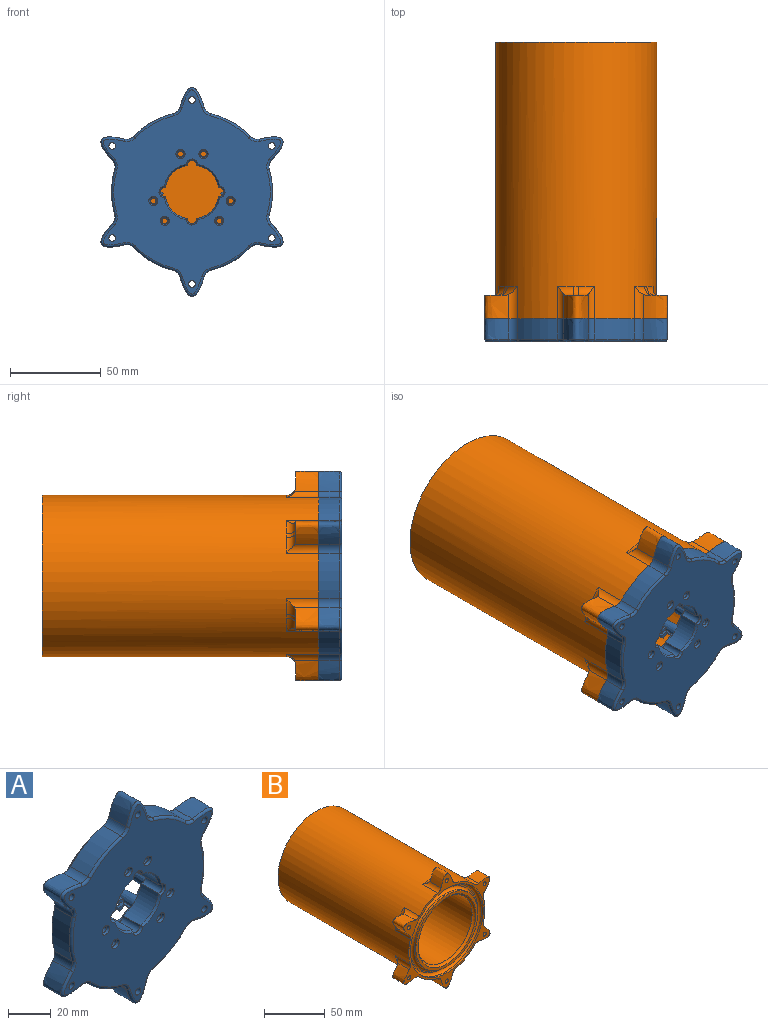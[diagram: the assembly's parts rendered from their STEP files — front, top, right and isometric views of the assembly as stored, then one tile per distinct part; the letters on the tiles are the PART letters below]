
ASSEMBLY  parts=2 mates=1
PART A: 221 faces, bbox 109.4x28x124.9 mm
  f0: plane 55.88x55.88mm, normal (0,1,0), area 1450.3mm2, adj f39,f42,f43,f44,f45,f46,f47,f48
  f1: cylinder r=44.45mm len=21.74mm, axis (0,-1,0), area 290.9mm2, adj f19,f21,f32,f78
  f2: extruded ~13.23x12.95mm, area 308.5mm2, adj f19,f21,f22,f74
  f3: cylinder r=44.45mm len=25.1mm, axis (0,-1,0), area 290.9mm2, adj f19,f22,f23,f70
  f4: extruded ~13.23x12.95mm, area 308.5mm2, adj f19,f23,f24,f66
  f5: cylinder r=44.45mm len=21.74mm, axis (0,-1,0), area 290.9mm2, adj f19,f24,f25,f62
  f6: extruded ~13.58x11.43mm, area 308.5mm2, adj f19,f25,f26,f58
  f7: cylinder r=44.45mm len=21.74mm, axis (0,-1,0), area 290.9mm2, adj f19,f26,f27,f57
  f8: extruded ~13.23x12.95mm, area 308.5mm2, adj f19,f27,f28,f61
  f9: cylinder r=44.45mm len=25.1mm, axis (0,-1,0), area 290.9mm2, adj f19,f28,f29,f65
  f10: extruded ~13.23x12.95mm, area 308.5mm2, adj f19,f29,f30,f69
  f11: cylinder r=44.45mm len=21.74mm, axis (0,-1,0), area 290.9mm2, adj f19,f30,f31,f73
  f12: cylinder r=1.84mm len=12.7mm, axis (0,-1,0), area 146.9mm2, adj f19,f20
  f13: cylinder r=1.84mm len=12.7mm, axis (0,-1,0), area 146.9mm2, adj f19,f20
  f14: cylinder r=1.84mm len=12.7mm, axis (0,-1,0), area 146.9mm2, adj f19,f20
  f15: cylinder r=1.84mm len=12.7mm, axis (0,-1,0), area 146.9mm2, adj f19,f20
  f16: cylinder r=1.84mm len=12.7mm, axis (0,-1,0), area 146.9mm2, adj f19,f20
  f17: extruded ~13.58x11.43mm, area 308.5mm2, adj f19,f31,f32,f77
  f18: cylinder r=1.84mm len=12.7mm, axis (0,-1,0), area 146.9mm2, adj f19,f20
  f19: plane 123.55x108.1mm, normal (0,1,0), area 1447.2mm2, adj f1,f2,f3,f4,f5,f6,f7,f8
  f20: plane 112.75x97.91mm, normal (0,-1,0), area 5549.7mm2, adj f12,f13,f14,f15,f16,f18,f56,f57
  f21: cylinder r=5.08mm len=11.43mm, axis (0,-1,0), area 60mm2, adj f1,f2,f19,f76
  f22: cylinder r=5.08mm len=11.43mm, axis (0,-1,0), area 60mm2, adj f2,f3,f19,f72
  f23: cylinder r=5.08mm len=11.43mm, axis (0,-1,0), area 60mm2, adj f3,f4,f19,f68
  f24: cylinder r=5.08mm len=11.43mm, axis (0,-1,0), area 60mm2, adj f4,f5,f19,f64
  f25: cylinder r=5.08mm len=11.43mm, axis (0,-1,0), area 60mm2, adj f5,f6,f19,f60
  f26: cylinder r=5.08mm len=11.43mm, axis (0,-1,0), area 60mm2, adj f6,f7,f19,f56
  f27: cylinder r=5.08mm len=11.43mm, axis (0,-1,0), area 60mm2, adj f7,f8,f19,f59
  f28: cylinder r=5.08mm len=11.43mm, axis (0,-1,0), area 60mm2, adj f8,f9,f19,f63
  f29: cylinder r=5.08mm len=11.43mm, axis (0,-1,0), area 60mm2, adj f9,f10,f19,f67
  f30: cylinder r=5.08mm len=11.43mm, axis (0,-1,0), area 60mm2, adj f10,f11,f19,f71
  f31: cylinder r=5.08mm len=11.43mm, axis (0,-1,0), area 60mm2, adj f11,f17,f19,f75
  f32: cylinder r=5.08mm len=11.43mm, axis (0,-1,0), area 60mm2, adj f1,f17,f19,f79
  f33: cylinder r=41.91mm len=83.82mm, axis (0,-1,0), area 200.7mm2, adj f19,f37
  f34: cylinder r=36.83mm len=73.66mm, axis (0,-1,0), area 176.3mm2, adj f36,f38
  f35: plane 78.99x78.99mm, normal (0,1,0), area 62.8mm2, adj f37,f38
  f36: plane 73.66x73.66mm, normal (0,1,0), area 1094.5mm2, adj f34,f40
  f37: torus R=39.5mm, axis (0,1,0), area 977.2mm2, adj f33,f35
  f38: torus R=39.24mm, axis (0,1,0), area 898mm2, adj f34,f35
  f39: cylinder r=27.94mm len=55.88mm, axis (0,-1,0), area 1783.6mm2, adj f0,f41
  f40: cylinder r=31.75mm len=63.5mm, axis (0,-1,0), area 1782.2mm2, adj f36,f220
  f41: plane 61.05x61.05mm, normal (0,1,0), area 474.5mm2, adj f39,f220
  f42: cylinder r=2.54mm len=11.43mm, axis (0,-1,0), area 96.2mm2, adj f0,f43,f49,f89
  f43: cylinder r=14.94mm len=12.19mm, axis (0,-1,0), area 210mm2, adj f0,f42,f44,f87
  f44: cylinder r=2.54mm len=11.43mm, axis (0,-1,0), area 96.2mm2, adj f0,f43,f45,f85
  f45: cylinder r=14.94mm len=12.19mm, axis (0,-1,0), area 210mm2, adj f0,f44,f46,f83
  f46: cylinder r=2.54mm len=11.43mm, axis (0,-1,0), area 96.2mm2, adj f0,f45,f47,f84
  f47: cylinder r=14.94mm len=12.19mm, axis (0,-1,0), area 210mm2, adj f0,f46,f48,f86
  f48: cylinder r=2.54mm len=11.43mm, axis (0,-1,0), area 96.2mm2, adj f0,f47,f49,f88
  f49: cylinder r=14.94mm len=12.19mm, axis (0,-1,0), area 210mm2, adj f0,f42,f48,f90
  f50: cylinder r=1.78mm len=11.43mm, axis (0,1,0), area 127.7mm2, adj f0,f80,f95
  f51: cylinder r=1.78mm len=11.43mm, axis (0,1,0), area 127.7mm2, adj f0,f92,f200
  f52: cylinder r=1.78mm len=11.43mm, axis (0,1,0), area 127.7mm2, adj f0,f91,f116
  f53: cylinder r=1.78mm len=11.43mm, axis (0,1,0), area 127.7mm2, adj f0,f82,f137
  f54: cylinder r=1.78mm len=11.43mm, axis (0,1,0), area 127.7mm2, adj f0,f81,f158
  f55: cylinder r=1.78mm len=11.43mm, axis (0,1,0), area 127.7mm2, adj f0,f93,f179
  f56: torus R=6.35mm, axis (0,-1,0), area 11.4mm2, adj f20,f26,f57,f58
  f57: torus R=43.18mm, axis (0,-1,0), area 50.2mm2, adj f7,f20,f56,f59
  f58: bspline ~14.43x12.79mm, area 51.6mm2, adj f6,f20,f56,f60
  f59: torus R=6.35mm, axis (0,-1,0), area 11.4mm2, adj f20,f27,f57,f61
  f60: torus R=6.35mm, axis (0,-1,0), area 11.4mm2, adj f20,f25,f58,f62
  f61: bspline ~14.68x14.01mm, area 51.6mm2, adj f8,f20,f59,f63
  f62: torus R=43.18mm, axis (0,-1,0), area 50.2mm2, adj f5,f20,f60,f64
  f63: torus R=6.35mm, axis (0,-1,0), area 11.4mm2, adj f20,f28,f61,f65
  f64: torus R=6.35mm, axis (0,-1,0), area 11.4mm2, adj f20,f24,f62,f66
  f65: torus R=43.18mm, axis (0,-1,0), area 50.2mm2, adj f9,f20,f63,f67
  f66: bspline ~14.04x13.58mm, area 51.6mm2, adj f4,f20,f64,f68
  f67: torus R=6.35mm, axis (0,-1,0), area 11.4mm2, adj f20,f29,f65,f69
  f68: torus R=6.35mm, axis (0,-1,0), area 11.4mm2, adj f20,f23,f66,f70
  f69: bspline ~14.04x13.58mm, area 51.6mm2, adj f10,f20,f67,f71
  f70: torus R=43.18mm, axis (0,-1,0), area 50.2mm2, adj f3,f20,f68,f72
  f71: torus R=6.35mm, axis (0,-1,0), area 11.4mm2, adj f20,f30,f69,f73
  f72: torus R=6.35mm, axis (0,-1,0), area 11.4mm2, adj f20,f22,f70,f74
  f73: torus R=43.18mm, axis (0,-1,0), area 50.2mm2, adj f11,f20,f71,f75
  f74: bspline ~14.01x13.59mm, area 51.6mm2, adj f2,f20,f72,f76
  f75: torus R=6.35mm, axis (0,-1,0), area 11.4mm2, adj f20,f31,f73,f77
  f76: torus R=6.35mm, axis (0,-1,0), area 11.4mm2, adj f20,f21,f74,f78
  f77: bspline ~14.43x12.79mm, area 51.6mm2, adj f17,f20,f75,f79
  f78: torus R=43.18mm, axis (0,-1,0), area 50.2mm2, adj f1,f20,f76,f79
  f79: torus R=6.35mm, axis (0,-1,0), area 11.4mm2, adj f20,f32,f77,f78
  f80: cone r=1.78mm half-angle=30deg, axis (0,-1,0), area 19.8mm2, adj f20,f50
  f81: cone r=1.78mm half-angle=30deg, axis (0,-1,0), area 19.8mm2, adj f20,f54
  f82: cone r=1.78mm half-angle=30deg, axis (0,-1,0), area 19.8mm2, adj f20,f53
  f83: cone r=14.94mm half-angle=30deg, axis (0,-1,0), area 26.7mm2, adj f20,f45,f84,f85
  f84: cone r=2.54mm half-angle=30deg, axis (0,-1,0), area 13.2mm2, adj f20,f46,f83,f86
  f85: cone r=2.54mm half-angle=30deg, axis (0,-1,0), area 13.2mm2, adj f20,f44,f83,f87
  f86: cone r=14.94mm half-angle=30deg, axis (0,-1,0), area 26.7mm2, adj f20,f47,f84,f88
  f87: cone r=14.94mm half-angle=30deg, axis (0,-1,0), area 26.7mm2, adj f20,f43,f85,f89
  f88: cone r=2.54mm half-angle=30deg, axis (0,-1,0), area 13.2mm2, adj f20,f48,f86,f90
  f89: cone r=2.54mm half-angle=30deg, axis (0,-1,0), area 13.2mm2, adj f20,f42,f87,f90
  f90: cone r=14.94mm half-angle=30deg, axis (0,-1,0), area 26.7mm2, adj f20,f49,f88,f89
  f91: cone r=1.78mm half-angle=30deg, axis (0,-1,0), area 19.8mm2, adj f20,f52
  f92: cone r=1.78mm half-angle=30deg, axis (0,-1,0), area 19.8mm2, adj f20,f51
  f93: cone r=1.78mm half-angle=30deg, axis (0,-1,0), area 19.8mm2, adj f20,f55
  f94: bspline ~13.97x7.67mm, area 268mm2, adj f0,f96,f97,f98,f106,f108,f109,f110
  f95: bspline ~13.97x3.58mm, area 87.4mm2, adj f50,f97,f98,f99,f100
  f96: plane 9.94x9.5mm, normal (0,1,0), area 32.9mm2, adj f94,f97,f98,f102,f103,f104,f105,f107
  f97: bspline ~13.97x1.99mm, area 24.9mm2, adj f0,f94,f95,f96,f101
  f98: bspline ~13.97x1.72mm, area 22.7mm2, adj f0,f94,f95,f96,f106,f107
  f99: plane 3.24x3.24mm, normal (0,-1,0), area 0.8mm2, adj f95,f100,f101,f102,f103,f104
  f100: plane 5.11x0.07mm, normal (-0.66,0,-0.75), area 0.2mm2, adj f95,f99,f104
  f101: plane 5.11x0.09mm, normal (0.88,0,0.47), area 0.2mm2, adj f97,f99,f102
  f102: extruded ~5.11x0.94mm, area 4.9mm2, adj f96,f99,f101,f103
  f103: extruded ~5.11x3.04mm, area 35.3mm2, adj f96,f99,f102,f104
  f104: extruded ~5.11x0.86mm, area 4.8mm2, adj f96,f99,f100,f103
  f105: plane 5.11x1.61mm, normal (0.75,0,-0.66), area 11mm2, adj f96,f106,f107,f108
  f106: plane 4.3x3.36mm, normal (0,-1,0), area 5.9mm2, adj f94,f98,f105,f107,f108
  f107: plane 5.25x3.01mm, normal (-0.66,0,-0.75), area 13.3mm2, adj f96,f98,f105,f106,f114
  f108: plane 5.11x3.51mm, normal (0.47,0,0.88), area 13.4mm2, adj f94,f96,f105,f106,f114
  f109: plane 3.91x2.87mm, normal (0,-1,0), area 6mm2, adj f94,f110,f111,f112
  f110: plane 6.42x4.45mm, normal (0.88,0,0.47), area 11.1mm2, adj f94,f96,f109,f111,f113
  f111: plane 5.11x1.9mm, normal (0.47,0,-0.88), area 11mm2, adj f96,f109,f110,f112
  f112: plane 5.11x3.85mm, normal (-0.97,0,-0.26), area 13.5mm2, adj f94,f96,f109,f111,f113
  f113: cylinder r=1.4mm len=3.07mm, axis (-0.97,0,-0.26), area 12.5mm2, adj f110,f112
  f114: cylinder r=1.4mm len=3.44mm, axis (0.47,0,0.88), area 15.3mm2, adj f107,f108
  f115: bspline ~13.97x7.67mm, area 268mm2, adj f0,f117,f118,f119,f127,f129,f130,f131
  f116: bspline ~13.97x3.58mm, area 87.4mm2, adj f52,f118,f119,f120,f121
  f117: plane 9.94x9.5mm, normal (0,1,0), area 32.9mm2, adj f115,f118,f119,f123,f124,f125,f126,f128
  f118: bspline ~13.97x1.99mm, area 24.9mm2, adj f0,f115,f116,f117,f122
  f119: bspline ~13.97x1.72mm, area 22.7mm2, adj f0,f115,f116,f117,f127,f128
  f120: plane 3.24x3.24mm, normal (0,-1,0), area 0.8mm2, adj f116,f121,f122,f123,f124,f125
  f121: plane 5.11x0.07mm, normal (0.66,0,-0.75), area 0.2mm2, adj f116,f120,f125
  f122: plane 5.11x0.09mm, normal (-0.88,0,0.47), area 0.2mm2, adj f118,f120,f123
  f123: extruded ~5.11x0.94mm, area 4.9mm2, adj f117,f120,f122,f124
  f124: extruded ~5.11x3.04mm, area 35.3mm2, adj f117,f120,f123,f125
  f125: extruded ~5.11x0.86mm, area 4.8mm2, adj f117,f120,f121,f124
  f126: plane 5.11x1.61mm, normal (-0.75,0,-0.66), area 11mm2, adj f117,f127,f128,f129
  f127: plane 4.3x3.36mm, normal (0,-1,0), area 5.9mm2, adj f115,f119,f126,f128,f129
  f128: plane 5.25x3.01mm, normal (0.66,0,-0.75), area 13.3mm2, adj f117,f119,f126,f127,f135
  f129: plane 5.11x3.51mm, normal (-0.47,0,0.88), area 13.4mm2, adj f115,f117,f126,f127,f135
  f130: plane 3.91x2.87mm, normal (0,-1,0), area 6mm2, adj f115,f131,f132,f133
  f131: plane 6.42x4.45mm, normal (-0.88,0,0.47), area 11.1mm2, adj f115,f117,f130,f132,f134
  f132: plane 5.11x1.9mm, normal (-0.47,0,-0.88), area 11mm2, adj f117,f130,f131,f133
  f133: plane 5.11x3.85mm, normal (0.97,0,-0.26), area 13.5mm2, adj f115,f117,f130,f132,f134
  f134: cylinder r=1.4mm len=3.07mm, axis (0.97,0,-0.26), area 12.5mm2, adj f131,f133
  f135: cylinder r=1.4mm len=3.44mm, axis (-0.47,0,0.88), area 15.3mm2, adj f128,f129
  f136: bspline ~13.97x7.67mm, area 268mm2, adj f0,f138,f139,f140,f148,f150,f151,f152
  f137: bspline ~13.97x3.57mm, area 87.4mm2, adj f53,f139,f140,f141,f142
  f138: plane 9.64x7.29mm, normal (0,1,0), area 32.9mm2, adj f136,f139,f140,f144,f145,f146,f147,f149
  f139: bspline ~13.97x2.29mm, area 24.9mm2, adj f0,f136,f137,f138,f143
  f140: bspline ~13.97x2.17mm, area 22.7mm2, adj f0,f136,f137,f138,f148,f149
  f141: plane 3.24x3.23mm, normal (0,-1,0), area 0.8mm2, adj f137,f142,f143,f144,f145,f146
  f142: plane 5.11x0.09mm, normal (-0.31,0,0.95), area 0.2mm2, adj f137,f141,f146
  f143: plane 5.11x0.1mm, normal (-0.03,0,-1), area 0.2mm2, adj f139,f141,f144
  f144: extruded ~5.11x0.87mm, area 4.9mm2, adj f138,f141,f143,f145
  f145: extruded ~5.11x3.05mm, area 35.3mm2, adj f138,f141,f144,f146
  f146: extruded ~5.11x0.7mm, area 4.8mm2, adj f138,f141,f142,f145
  f147: plane 5.11x2.05mm, normal (-0.95,0,-0.31), area 11mm2, adj f138,f148,f149,f150
  f148: plane 3.82x3.26mm, normal (0,-1,0), area 5.9mm2, adj f136,f140,f147,f149,f150
  f149: plane 5.25x3.78mm, normal (-0.31,0,0.95), area 13.3mm2, adj f138,f140,f147,f148,f156
  f150: plane 5.11x3.38mm, normal (0.53,0,-0.85), area 13.4mm2, adj f136,f138,f147,f148,f156
  f151: plane 3.64x2.26mm, normal (0,-1,0), area 6mm2, adj f136,f152,f153,f154
  f152: plane 6.42x4.87mm, normal (-0.03,0,-1), area 11.1mm2, adj f136,f138,f151,f153,f155
  f153: plane 5.11x2.16mm, normal (-1,0,0.03), area 11mm2, adj f138,f151,f152,f154
  f154: plane 5.11x3.85mm, normal (0.26,0,0.97), area 13.5mm2, adj f136,f138,f151,f153,f155
  f155: cylinder r=1.4mm len=3.07mm, axis (0.26,0,0.97), area 12.5mm2, adj f152,f154
  f156: cylinder r=1.4mm len=3.47mm, axis (0.53,0,-0.85), area 15.3mm2, adj f149,f150
  f157: bspline ~13.97x7.67mm, area 268mm2, adj f0,f159,f160,f161,f169,f171,f172,f173
  f158: bspline ~13.97x3.58mm, area 87.4mm2, adj f54,f160,f161,f162,f163
  f159: plane 9.97x8.45mm, normal (0,1,0), area 32.9mm2, adj f157,f160,f161,f165,f166,f167,f168,f170
  f160: bspline ~13.97x1.98mm, area 24.9mm2, adj f0,f157,f158,f159,f164
  f161: bspline ~13.97x2.24mm, area 22.7mm2, adj f0,f157,f158,f159,f169,f170
  f162: plane 3.24x3.24mm, normal (0,-1,0), area 0.8mm2, adj f158,f163,f164,f165,f166,f167
  f163: plane 5.11x0.09mm, normal (-0.98,0,-0.2), area 0.2mm2, adj f158,f162,f167
  f164: plane 5.11x0.08mm, normal (0.85,0,0.52), area 0.2mm2, adj f160,f162,f165
  f165: extruded ~5.11x0.77mm, area 4.9mm2, adj f159,f162,f164,f166
  f166: extruded ~5.11x3.05mm, area 35.3mm2, adj f159,f162,f165,f167
  f167: extruded ~5.11x0.9mm, area 4.8mm2, adj f159,f162,f163,f166
  f168: plane 5.11x2.11mm, normal (-0.2,0,0.98), area 11mm2, adj f159,f169,f170,f171
  f169: plane 4.2x2.12mm, normal (0,-1,0), area 5.9mm2, adj f157,f161,f168,f170,f171
  f170: plane 5.25x3.9mm, normal (-0.98,0,-0.2), area 13.3mm2, adj f159,f161,f168,f169,f177
  f171: plane 5.11x3.98mm, normal (1,0,-0.03), area 13.4mm2, adj f157,f159,f168,f169,f177
  f172: plane 3.76x3.56mm, normal (0,-1,0), area 6mm2, adj f157,f173,f174,f175
  f173: plane 6.42x4.34mm, normal (0.85,0,0.52), area 11.1mm2, adj f157,f159,f172,f174,f176
  f174: plane 5.11x1.84mm, normal (-0.52,0,0.85), area 11mm2, adj f159,f172,f173,f175
  f175: plane 5.11x2.82mm, normal (-0.71,0,-0.71), area 13.5mm2, adj f157,f159,f172,f174,f176
  f176: cylinder r=1.4mm len=2.98mm, axis (-0.71,0,-0.71), area 12.5mm2, adj f173,f175
  f177: cylinder r=1.4mm len=2.86mm, axis (1,0,-0.03), area 15.3mm2, adj f170,f171
  f178: bspline ~13.97x7.67mm, area 268mm2, adj f0,f180,f181,f182,f190,f192,f193,f194
  f179: bspline ~13.97x3.58mm, area 87.4mm2, adj f55,f181,f182,f183,f184
  f180: plane 9.97x8.45mm, normal (0,1,0), area 32.9mm2, adj f178,f181,f182,f186,f187,f188,f189,f191
  f181: bspline ~13.97x1.98mm, area 24.9mm2, adj f0,f178,f179,f180,f185
  f182: bspline ~13.97x2.24mm, area 22.7mm2, adj f0,f178,f179,f180,f190,f191
  f183: plane 3.24x3.24mm, normal (0,-1,0), area 0.8mm2, adj f179,f184,f185,f186,f187,f188
  f184: plane 5.11x0.09mm, normal (0.98,0,-0.2), area 0.2mm2, adj f179,f183,f188
  f185: plane 5.11x0.08mm, normal (-0.85,0,0.52), area 0.2mm2, adj f181,f183,f186
  f186: extruded ~5.11x0.77mm, area 4.9mm2, adj f180,f183,f185,f187
  f187: extruded ~5.11x3.05mm, area 35.3mm2, adj f180,f183,f186,f188
  f188: extruded ~5.11x0.9mm, area 4.8mm2, adj f180,f183,f184,f187
  f189: plane 5.11x2.11mm, normal (0.2,0,0.98), area 11mm2, adj f180,f190,f191,f192
  f190: plane 4.2x2.12mm, normal (0,-1,0), area 5.9mm2, adj f178,f182,f189,f191,f192
  f191: plane 5.25x3.9mm, normal (0.98,0,-0.2), area 13.3mm2, adj f180,f182,f189,f190,f198
  f192: plane 5.11x3.98mm, normal (-1,0,-0.03), area 13.4mm2, adj f178,f180,f189,f190,f198
  f193: plane 3.76x3.56mm, normal (0,-1,0), area 6mm2, adj f178,f194,f195,f196
  f194: plane 6.42x4.34mm, normal (-0.85,0,0.52), area 11.1mm2, adj f178,f180,f193,f195,f197
  f195: plane 5.11x1.84mm, normal (0.52,0,0.85), area 11mm2, adj f180,f193,f194,f196
  f196: plane 5.11x2.82mm, normal (0.71,0,-0.71), area 13.5mm2, adj f178,f180,f193,f195,f197
  f197: cylinder r=1.4mm len=2.98mm, axis (0.71,0,-0.71), area 12.5mm2, adj f194,f196
  f198: cylinder r=1.4mm len=2.86mm, axis (-1,0,-0.03), area 15.3mm2, adj f191,f192
  f199: bspline ~13.97x7.67mm, area 268mm2, adj f0,f201,f202,f203,f211,f213,f214,f215
  f200: bspline ~13.97x3.57mm, area 87.4mm2, adj f51,f202,f203,f204,f205
  f201: plane 9.64x7.29mm, normal (0,1,0), area 32.9mm2, adj f199,f202,f203,f207,f208,f209,f210,f212
  f202: bspline ~13.97x2.29mm, area 24.9mm2, adj f0,f199,f200,f201,f206
  f203: bspline ~13.97x2.17mm, area 22.7mm2, adj f0,f199,f200,f201,f211,f212
  f204: plane 3.24x3.23mm, normal (0,-1,0), area 0.8mm2, adj f200,f205,f206,f207,f208,f209
  f205: plane 5.11x0.09mm, normal (0.31,0,0.95), area 0.2mm2, adj f200,f204,f209
  f206: plane 5.11x0.1mm, normal (0.03,0,-1), area 0.2mm2, adj f202,f204,f207
  f207: extruded ~5.11x0.87mm, area 4.9mm2, adj f201,f204,f206,f208
  f208: extruded ~5.11x3.05mm, area 35.3mm2, adj f201,f204,f207,f209
  f209: extruded ~5.11x0.7mm, area 4.8mm2, adj f201,f204,f205,f208
  f210: plane 5.11x2.05mm, normal (0.95,0,-0.31), area 11mm2, adj f201,f211,f212,f213
  f211: plane 3.82x3.26mm, normal (0,-1,0), area 5.9mm2, adj f199,f203,f210,f212,f213
  f212: plane 5.25x3.78mm, normal (0.31,0,0.95), area 13.3mm2, adj f201,f203,f210,f211,f219
  f213: plane 5.11x3.38mm, normal (-0.53,0,-0.85), area 13.4mm2, adj f199,f201,f210,f211,f219
  f214: plane 3.64x2.26mm, normal (0,-1,0), area 6mm2, adj f199,f215,f216,f217
  f215: plane 6.42x4.87mm, normal (0.03,0,-1), area 11.1mm2, adj f199,f201,f214,f216,f218
  f216: plane 5.11x2.16mm, normal (1,0,0.03), area 11mm2, adj f201,f214,f215,f217
  f217: plane 5.11x3.85mm, normal (-0.26,0,0.97), area 13.5mm2, adj f199,f201,f214,f216,f218
  f218: cylinder r=1.4mm len=3.07mm, axis (-0.26,0,0.97), area 12.5mm2, adj f215,f217
  f219: cylinder r=1.4mm len=3.47mm, axis (-0.53,0,-0.85), area 15.3mm2, adj f212,f213
  f220: torus R=30.52mm, axis (0,1,0), area 378.9mm2, adj f40,f41
PART B: 62 faces, bbox 108.1x152.5x123.5 mm
  f0: cylinder r=31.75mm len=128.81mm, axis (0,-1,0), area 25696.6mm2, adj f3,f4
  f1: plane 57.15x57.15mm, normal (0,-1,0), area 2565.2mm2, adj f2
  f2: cylinder r=28.57mm len=57.15mm, axis (0,1,0), area 114mm2, adj f1,f3
  f3: torus R=26.67mm, axis (0,1,0), area 1160.3mm2, adj f0,f2
  f4: torus R=30.99mm, axis (0,-1,0), area 653.7mm2, adj f0,f5
  f5: plane 72.39x72.39mm, normal (0,-1,0), area 584.3mm2, adj f4,f6
  f6: cylinder r=36.2mm len=72.39mm, axis (0,-1,0), area 433.2mm2, adj f5,f60
  f7: plane 80.01x80.01mm, normal (0,-1,0), area 314.2mm2, adj f60,f61
  f8: cylinder r=42.55mm len=85.09mm, axis (0,-1,0), area 509.2mm2, adj f59,f61
  f9: plane 17.28x16.68mm, normal (0,1,0), area 54.9mm2, adj f27,f29,f34,f42
  f10: plane 17.28x16.68mm, normal (0,1,0), area 54.9mm2, adj f24,f26,f35,f45
  f11: plane 15.24x14.83mm, normal (0,1,0), area 54.9mm2, adj f21,f23,f36,f48
  f12: plane 17.28x16.68mm, normal (0,1,0), area 54.9mm2, adj f18,f20,f37,f51
  f13: plane 17.28x16.68mm, normal (0,1,0), area 54.9mm2, adj f15,f17,f38,f54
  f14: plane 88.9x88.9mm, normal (0,1,0), area 6207.2mm2, adj f56
  f15: torus R=49.53mm, axis (0,-1,0), area 52.1mm2, adj f13,f16,f54,f55,f56
  f16: bspline ~5.65x5.08mm, area 18.6mm2, adj f15,f17,f38,f56
  f17: torus R=49.53mm, axis (0,-1,0), area 52.1mm2, adj f13,f16,f53,f54,f56
  f18: torus R=49.53mm, axis (0,-1,0), area 52.1mm2, adj f12,f19,f51,f52,f56
  f19: bspline ~5.65x5.08mm, area 18.6mm2, adj f18,f20,f37,f56
  f20: torus R=49.53mm, axis (0,-1,0), area 52.1mm2, adj f12,f19,f50,f51,f56
  f21: torus R=49.53mm, axis (0,-1,0), area 52.1mm2, adj f11,f22,f48,f49,f56
  f22: bspline ~5.08x5.08mm, area 18.6mm2, adj f21,f23,f36,f56
  f23: torus R=49.53mm, axis (0,-1,0), area 52.1mm2, adj f11,f22,f47,f48,f56
  f24: torus R=49.53mm, axis (0,-1,0), area 52.1mm2, adj f10,f25,f45,f46,f56
  f25: bspline ~5.65x5.08mm, area 18.6mm2, adj f24,f26,f35,f56
  f26: torus R=49.53mm, axis (0,-1,0), area 52.1mm2, adj f10,f25,f44,f45,f56
  f27: torus R=49.53mm, axis (0,-1,0), area 52.1mm2, adj f9,f28,f42,f43,f56
  f28: bspline ~5.65x5.08mm, area 18.6mm2, adj f27,f29,f34,f56
  f29: torus R=49.53mm, axis (0,-1,0), area 52.1mm2, adj f9,f28,f41,f42,f56
  f30: bspline ~5.22x5.22mm, area 18.6mm2, adj f31,f32,f39,f56
  f31: torus R=49.53mm, axis (0,-1,0), area 52.1mm2, adj f30,f33,f40,f56,f58
  f32: torus R=49.53mm, axis (0,-1,0), area 52.1mm2, adj f30,f33,f56,f57,f58
  f33: plane 15.24x14.83mm, normal (0,1,0), area 54.9mm2, adj f31,f32,f39,f58
  f34: cylinder r=1.84mm len=12.7mm, axis (0,-1,0), area 146.9mm2, adj f9,f28,f59
  f35: cylinder r=1.84mm len=12.7mm, axis (0,-1,0), area 146.9mm2, adj f10,f25,f59
  f36: cylinder r=1.84mm len=12.7mm, axis (0,-1,0), area 146.9mm2, adj f11,f22,f59
  f37: cylinder r=1.84mm len=12.7mm, axis (0,-1,0), area 146.9mm2, adj f12,f19,f59
  f38: cylinder r=1.84mm len=12.7mm, axis (0,-1,0), area 146.9mm2, adj f13,f16,f59
  f39: cylinder r=1.84mm len=12.7mm, axis (0,-1,0), area 146.9mm2, adj f30,f33,f59
  f40: cylinder r=5.08mm len=17.78mm, axis (0,-1,0), area 80.3mm2, adj f31,f56,f58,f59
  f41: cylinder r=5.08mm len=17.78mm, axis (0,-1,0), area 80.3mm2, adj f29,f42,f56,f59
  f42: extruded ~13.3x13.23mm, area 344.4mm2, adj f9,f27,f29,f41,f43,f59
  f43: cylinder r=5.08mm len=17.78mm, axis (0,-1,0), area 80.3mm2, adj f27,f42,f56,f59
  f44: cylinder r=5.08mm len=17.78mm, axis (0,-1,0), area 80.3mm2, adj f26,f45,f56,f59
  f45: extruded ~13.3x13.23mm, area 344.4mm2, adj f10,f24,f26,f44,f46,f59
  f46: cylinder r=5.08mm len=17.78mm, axis (0,-1,0), area 80.3mm2, adj f24,f45,f56,f59
  f47: cylinder r=5.08mm len=17.78mm, axis (0,-1,0), area 80.3mm2, adj f23,f48,f56,f59
  f48: extruded ~13.58x13.3mm, area 344.4mm2, adj f11,f21,f23,f47,f49,f59
  f49: cylinder r=5.08mm len=17.78mm, axis (0,-1,0), area 80.3mm2, adj f21,f48,f56,f59
  f50: cylinder r=5.08mm len=17.78mm, axis (0,-1,0), area 80.3mm2, adj f20,f51,f56,f59
  f51: extruded ~13.3x13.23mm, area 344.4mm2, adj f12,f18,f20,f50,f52,f59
  f52: cylinder r=5.08mm len=17.78mm, axis (0,-1,0), area 80.3mm2, adj f18,f51,f56,f59
  f53: cylinder r=5.08mm len=17.78mm, axis (0,-1,0), area 80.3mm2, adj f17,f54,f56,f59
  f54: extruded ~13.3x13.23mm, area 344.4mm2, adj f13,f15,f17,f53,f55,f59
  f55: cylinder r=5.08mm len=17.78mm, axis (0,-1,0), area 80.3mm2, adj f15,f54,f56,f59
  f56: cylinder r=44.45mm len=152.4mm, axis (0,1,0), area 40312.7mm2, adj f14,f15,f16,f17,f18,f19,f20,f21
  f57: cylinder r=5.08mm len=17.78mm, axis (0,-1,0), area 80.3mm2, adj f32,f56,f58,f59
  f58: extruded ~13.58x13.3mm, area 344.4mm2, adj f31,f32,f33,f40,f57,f59
  f59: plane 123.55x108.1mm, normal (0,-1,0), area 1278.8mm2, adj f8,f34,f35,f36,f37,f38,f39,f40
  f60: torus R=38.73mm, axis (0,-1,0), area 930.5mm2, adj f6,f7
  f61: torus R=40mm, axis (0,-1,0), area 1043.4mm2, adj f7,f8
PLACE A t=(-3.94,-70.5,16.41)mm
PLACE B t=(-3.94,12.05,16.41)mm
MATE fastened A.f13 <-> B.f39  axis (0,1,0) through (-3.94,-64.15,67.21)mm
